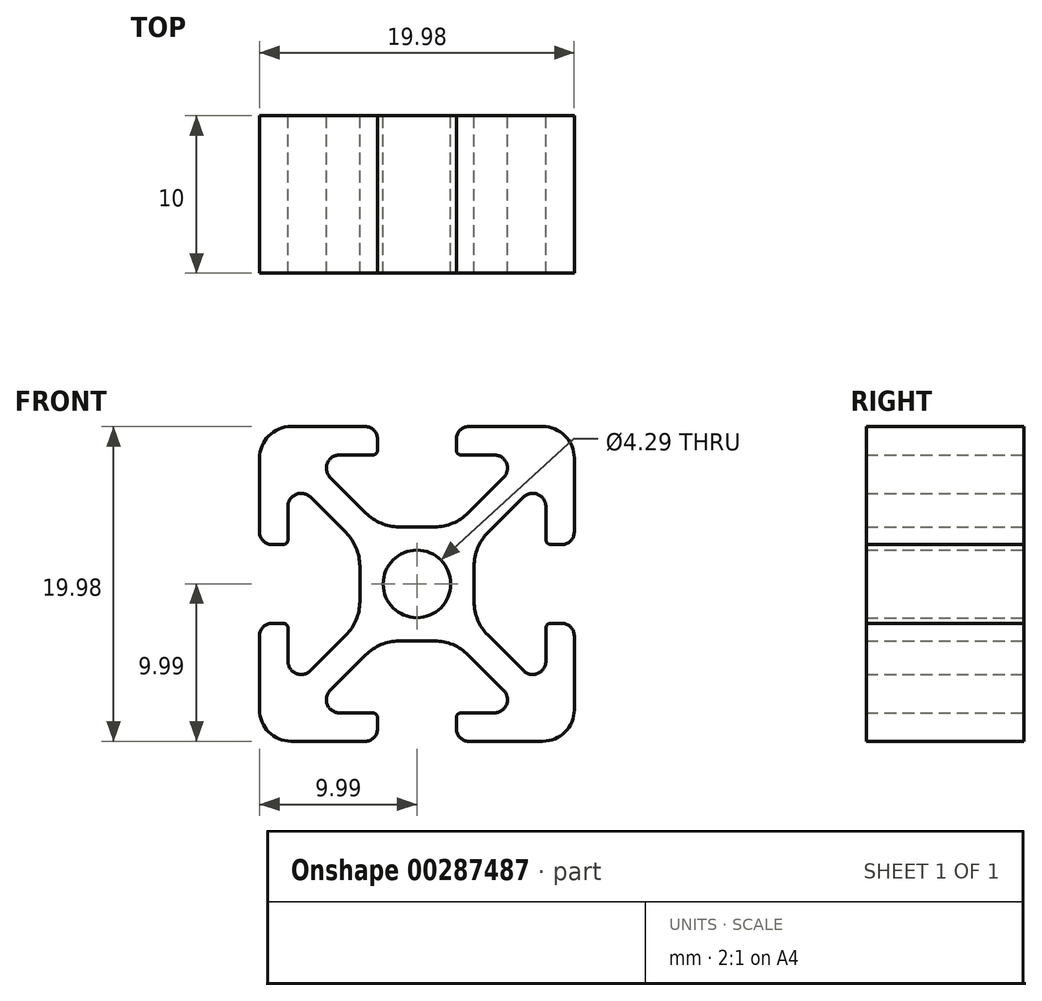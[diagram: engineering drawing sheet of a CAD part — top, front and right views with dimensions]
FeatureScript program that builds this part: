
annotation { "Feature Type Name" : "Feature", "Feature Type Description" : "" }
export const myFeature = defineFeature(function(context is Context, id is Id, definition is map)
    precondition{}
    {
        {
            var Q0;
            Q0=qCreatedBy(makeId("Front.planeOp"),FACE);
            var sketch = newSketch(context, id + "F0", { "sketchPlane" : qUnion([Q0])});
            skLineSegment(sketch, "E0", {"start": v(-7.99, 10) * mm, "end": v(-3.29, 10) * mm});
            skArc(sketch, "E1", {"start": v(-3.29, 10) * mm, "mid": v(-2.73, 9.76) * mm, "end": v(-2.5, 9.2) * mm});
            skLineSegment(sketch, "E2", {"start": v(-2.5, 9.2) * mm, "end": v(-2.5, 8.5) * mm});
            skLineSegment(sketch, "E3", {"start": v(-5.5, 6.76) * mm, "end": v(-3.25, 4.5) * mm});
            skArc(sketch, "E4", {"start": v(-4.91, 8.2) * mm, "mid": v(-5.69, 7.67) * mm, "end": v(-5.5, 6.76) * mm});
            skLineSegment(sketch, "E5", {"start": v(3.29, 10) * mm, "end": v(7.99, 10) * mm});
            skArc(sketch, "E6", {"start": v(2.5, 9.2) * mm, "mid": v(2.73, 9.76) * mm, "end": v(3.29, 10) * mm});
            skLineSegment(sketch, "E7", {"start": v(3.25, 4.5) * mm, "end": v(5.5, 6.76) * mm});
            skArc(sketch, "E8", {"start": v(1.13, 3.63) * mm, "mid": v(2.28, 3.86) * mm, "end": v(3.25, 4.5) * mm});
            skArc(sketch, "E9", {"start": v(7.99, 10) * mm, "mid": v(9.4, 9.4) * mm, "end": v(10, 7.99) * mm});
            skLineSegment(sketch, "E10", {"start": v(-2.8, 8.2) * mm, "end": v(-4.91, 8.2) * mm});
            skArc(sketch, "E11", {"start": v(-2.5, 8.5) * mm, "mid": v(-2.6, 8.28) * mm, "end": v(-2.8, 8.2) * mm});
            skLineSegment(sketch, "E12", {"start": v(4.91, 8.2) * mm, "end": v(2.8, 8.2) * mm});
            skLineSegment(sketch, "E13", {"start": v(2.5, 8.5) * mm, "end": v(2.5, 9.2) * mm});
            skArc(sketch, "E14", {"start": v(2.8, 8.2) * mm, "mid": v(2.6, 8.28) * mm, "end": v(2.5, 8.5) * mm});
            skArc(sketch, "E15", {"start": v(5.5, 6.76) * mm, "mid": v(5.69, 7.67) * mm, "end": v(4.91, 8.2) * mm});
            skLineSegment(sketch, "E16", {"start": v(-1.13, 3.63) * mm, "end": v(1.13, 3.63) * mm});
            skArc(sketch, "E17", {"start": v(-3.25, 4.5) * mm, "mid": v(-2.28, 3.86) * mm, "end": v(-1.13, 3.63) * mm});
            skArc(sketch, "E18", {"start": v(-10, 7.99) * mm, "mid": v(-9.4, 9.4) * mm, "end": v(-7.99, 10) * mm});
            skLineSegment(sketch, "E19", {"start": v(10, 7.99) * mm, "end": v(10, 3.29) * mm});
            skLineSegment(sketch, "E20", {"start": v(4.5, -3.25) * mm, "end": v(6.76, -5.5) * mm});
            skArc(sketch, "E21", {"start": v(3.63, -1.13) * mm, "mid": v(3.86, -2.28) * mm, "end": v(4.5, -3.25) * mm});
            skLineSegment(sketch, "E22", {"start": v(3.63, 1.13) * mm, "end": v(3.63, -1.13) * mm});
            skArc(sketch, "E23", {"start": v(9.2, -2.5) * mm, "mid": v(9.76, -2.73) * mm, "end": v(10, -3.29) * mm});
            skLineSegment(sketch, "E24", {"start": v(10, -3.29) * mm, "end": v(10, -7.99) * mm});
            skLineSegment(sketch, "E25", {"start": v(8.5, -2.5) * mm, "end": v(9.2, -2.5) * mm});
            skLineSegment(sketch, "E26", {"start": v(-9.2, -2.5) * mm, "end": v(-8.5, -2.5) * mm});
            skArc(sketch, "E27", {"start": v(-10, -3.29) * mm, "mid": v(-9.76, -2.73) * mm, "end": v(-9.2, -2.5) * mm});
            skLineSegment(sketch, "E28", {"start": v(-8.2, -2.8) * mm, "end": v(-8.2, -4.91) * mm});
            skLineSegment(sketch, "E29", {"start": v(-10, 3.29) * mm, "end": v(-10, 7.99) * mm});
            skArc(sketch, "E30", {"start": v(-9.2, 2.5) * mm, "mid": v(-9.76, 2.73) * mm, "end": v(-10, 3.29) * mm});
            skLineSegment(sketch, "E31", {"start": v(-4.5, 3.25) * mm, "end": v(-6.76, 5.5) * mm});
            skLineSegment(sketch, "E32", {"start": v(-3.63, -1.13) * mm, "end": v(-3.63, 1.13) * mm});
            skArc(sketch, "E33", {"start": v(-3.63, 1.13) * mm, "mid": v(-3.86, 2.28) * mm, "end": v(-4.5, 3.25) * mm});
            skArc(sketch, "E34", {"start": v(-6.76, 5.5) * mm, "mid": v(-7.67, 5.69) * mm, "end": v(-8.2, 4.91) * mm});
            skLineSegment(sketch, "E35", {"start": v(-8.5, 2.5) * mm, "end": v(-9.2, 2.5) * mm});
            skLineSegment(sketch, "E36", {"start": v(8.2, 2.8) * mm, "end": v(8.2, 4.91) * mm});
            skArc(sketch, "E37", {"start": v(8.2, 4.91) * mm, "mid": v(7.67, 5.69) * mm, "end": v(6.76, 5.5) * mm});
            skLineSegment(sketch, "E38", {"start": v(-10, -7.99) * mm, "end": v(-10, -3.29) * mm});
            skArc(sketch, "E39", {"start": v(-4.5, -3.25) * mm, "mid": v(-3.86, -2.28) * mm, "end": v(-3.63, -1.13) * mm});
            skLineSegment(sketch, "E40", {"start": v(-6.76, -5.5) * mm, "end": v(-4.5, -3.25) * mm});
            skLineSegment(sketch, "E41", {"start": v(1.13, -3.63) * mm, "end": v(-1.13, -3.63) * mm});
            skLineSegment(sketch, "E42", {"start": v(5.5, -6.76) * mm, "end": v(3.25, -4.5) * mm});
            skArc(sketch, "E43", {"start": v(3.25, -4.5) * mm, "mid": v(2.28, -3.86) * mm, "end": v(1.13, -3.63) * mm});
            skLineSegment(sketch, "E44", {"start": v(8.2, -4.91) * mm, "end": v(8.2, -2.8) * mm});
            skLineSegment(sketch, "E45", {"start": v(-4.91, -8.2) * mm, "end": v(-2.8, -8.2) * mm});
            skArc(sketch, "E46", {"start": v(-5.5, -6.76) * mm, "mid": v(-5.69, -7.67) * mm, "end": v(-4.91, -8.2) * mm});
            skArc(sketch, "E47", {"start": v(-8.2, -4.91) * mm, "mid": v(-7.67, -5.69) * mm, "end": v(-6.76, -5.5) * mm});
            skArc(sketch, "E48", {"start": v(-8.5, -2.5) * mm, "mid": v(-8.28, -2.6) * mm, "end": v(-8.2, -2.8) * mm});
            skArc(sketch, "E49", {"start": v(4.91, -8.2) * mm, "mid": v(5.69, -7.67) * mm, "end": v(5.5, -6.76) * mm});
            skLineSegment(sketch, "E50", {"start": v(2.5, -9.2) * mm, "end": v(2.5, -8.5) * mm});
            skArc(sketch, "E51", {"start": v(2.5, -8.5) * mm, "mid": v(2.6, -8.28) * mm, "end": v(2.8, -8.2) * mm});
            skLineSegment(sketch, "E52", {"start": v(2.8, -8.2) * mm, "end": v(4.91, -8.2) * mm});
            skArc(sketch, "E53", {"start": v(3.29, -10) * mm, "mid": v(2.73, -9.76) * mm, "end": v(2.5, -9.2) * mm});
            skArc(sketch, "E54", {"start": v(6.76, -5.5) * mm, "mid": v(7.67, -5.69) * mm, "end": v(8.2, -4.91) * mm});
            skArc(sketch, "E55", {"start": v(10, -7.99) * mm, "mid": v(9.4, -9.4) * mm, "end": v(7.99, -10) * mm});
            skArc(sketch, "E56", {"start": v(4.5, 3.25) * mm, "mid": v(3.86, 2.28) * mm, "end": v(3.63, 1.13) * mm});
            skLineSegment(sketch, "E57", {"start": v(-3.25, -4.5) * mm, "end": v(-5.5, -6.76) * mm});
            skLineSegment(sketch, "E58", {"start": v(-2.5, -8.5) * mm, "end": v(-2.5, -9.2) * mm});
            skArc(sketch, "E59", {"start": v(-2.8, -8.2) * mm, "mid": v(-2.6, -8.28) * mm, "end": v(-2.5, -8.5) * mm});
            skArc(sketch, "E60", {"start": v(-2.5, -9.2) * mm, "mid": v(-2.73, -9.76) * mm, "end": v(-3.29, -10) * mm});
            skArc(sketch, "E61", {"start": v(-1.13, -3.63) * mm, "mid": v(-2.28, -3.86) * mm, "end": v(-3.25, -4.5) * mm});
            skArc(sketch, "E62", {"start": v(10, 3.29) * mm, "mid": v(9.76, 2.73) * mm, "end": v(9.2, 2.5) * mm});
            skLineSegment(sketch, "E63", {"start": v(6.76, 5.5) * mm, "end": v(4.5, 3.25) * mm});
            skLineSegment(sketch, "E64", {"start": v(-8.2, 4.91) * mm, "end": v(-8.2, 2.8) * mm});
            skLineSegment(sketch, "E65", {"start": v(-3.29, -10) * mm, "end": v(-7.99, -10) * mm});
            skArc(sketch, "E66", {"start": v(-7.99, -10) * mm, "mid": v(-9.4, -9.4) * mm, "end": v(-10, -7.99) * mm});
            skLineSegment(sketch, "E67", {"start": v(7.99, -10) * mm, "end": v(3.29, -10) * mm});
            skLineSegment(sketch, "E68", {"start": v(9.2, 2.5) * mm, "end": v(8.5, 2.5) * mm});
            skArc(sketch, "E69", {"start": v(8.5, 2.5) * mm, "mid": v(8.28, 2.6) * mm, "end": v(8.2, 2.8) * mm});
            skCircle(sketch, "E70", {"center": v(0, 0) * mm, "radius": 2.15 * mm});
            skArc(sketch, "E71", {"start": v(-8.2, 2.8) * mm, "mid": v(-8.28, 2.6) * mm, "end": v(-8.5, 2.5) * mm});
            skArc(sketch, "E72", {"start": v(8.2, -2.8) * mm, "mid": v(8.28, -2.6) * mm, "end": v(8.5, -2.5) * mm});
            skSolve(sketch);
        }
        {
            var Q0;
            Q0 = qSketchRegion(id + "F0", true);
            extrude(context, id + "F1", {"entities" : qUnion([Q0]), "depth" : 10 * mm});
        }
    });
